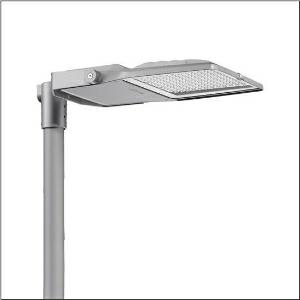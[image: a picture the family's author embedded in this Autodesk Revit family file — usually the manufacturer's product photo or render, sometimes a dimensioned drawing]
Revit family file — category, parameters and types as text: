
# Revit family: floodlight_fl_21_iq_midi___pl43_5xa7781e2a3a_1390
name_source: partatom
category: Lighting Fixtures
units: mm (PartAtom-declared; Revit-internal decimal feet)

## family parameters
Cut with Voids When Loaded = No
Host = Face
Light Source = No
Part Type = Normal
Room Calculation Point = No
Round Connector Dimension = Use Diameter
Shared = No

## types (1)
- --- (1 x LED, 27540 lm, 208.1 W, 3000K)
    Apparent Load = 208 VA
    CIE Flux Codes = 27 78 99 100 100
    Color Rendering = 70
    Color Temperature = 3000K
    Default Elevation = 1800 mm
    Description = Floodlight FL 21 iQ midi, floodlight, primary light control with lens, of PMMA, primary optical cover: protective disc, of toughened safety glass, transparent, light distribution: PL43, light emission: direct distribution, installation type: surface-mounted, LED, High Power LED, rated luminous flux: 27.540lm, luminous efficacy: 132lm/W, light colour: 730, colour temperature: 3000K, control gear: iQ Comfort/DALI, control: optimised constant luminous flux control (CLO 2.0), Desk-Remote (wireless, voltage-free reading and setting of iQ features in the workshop via application-optimized NFC function/RFID function), Light-Fading, Smart-Wire, Night-Set, Lumen-Switch, Temp-Guard, Auto-Match, with terminal, 6-pole, mains connection: 220..240V, AC, 50/60Hz, start of lifetime: 208W, end of service life: 227W, reduction: 90W, luminaire housing, of diecast aluminium, powder-coated, Siteco® metallic grey (DB 702S), corrosivity category C5 mid according to DIN EN ISO 12944, suitable for swimming pools, chlorine-resistant, sealing non-destructively replaceable, please order mast flange separately, mast bracket, of steel, galvanised, powder-coated, Siteco® metallic grey (DB 702S), protection rating (complete): IP66, insulation class (complete): insulation class II (safety insulation), certification: CE, ENEC, VDE, protection symbol: D, impact resistance: IK08, permissible operating ambient temperature: -40..+40°C, permissible operating ambient temperature for outdoor applications: -40..+50°C, standard: DIN EN 12944, LABS conformity tested according to VDMA 24364:2018-05, packaging unit: 1 piece

Light Distribution: PL43
    Height = 76 mm
    Lamp = 1 x LED
    Lamp Light Flux = 27540 lm
    Lamp Power = 208.1 W
    Lamp count = 1
    Length = 657 mm
    Luminous efficacy = 132 lm/W
    Manufacturer = Siteco
    ModVariant = No
    Model = 5XA7781E2A3A
    Number of Poles = 1
    OnlyDefault = Yes
    Power Factor = 1
    Product Name = Floodlight FL 21 iQ midi | PL43
    Product group = floodlight | pylon annexe
    ProductGroupID = 6201
    Protection Class = Protection class II
    Protection Degree = IP 66
    RLX_Detail_Level = 1
    RLX_Emergency_Light_Flux = 0 lm
    RLX_Emergency_Type = 0
    RLX_Emergency_Type_DB = No
    RlxData = <blob elided: 153769 chars, md5=5d6f7080>
    Socket = socket
    Standby Power = 0 W
    System Light Flux = 27540 lm
    System Power = 208 W
    Type Comments = factory setting: luminous flux: 100 % | dim-lin: 254 | 710 mA
    Type Image = l_1007123.jpg
    URL = http://relux.com
    VarID = @adj_126809
    Voltage = 0 V
    Weight = 0.00 kg
    Width = 442 mm

## geometry (parser evidence)
native form markers: Blend x4, Sweep x11
no freeform markers — native parametric forms only
